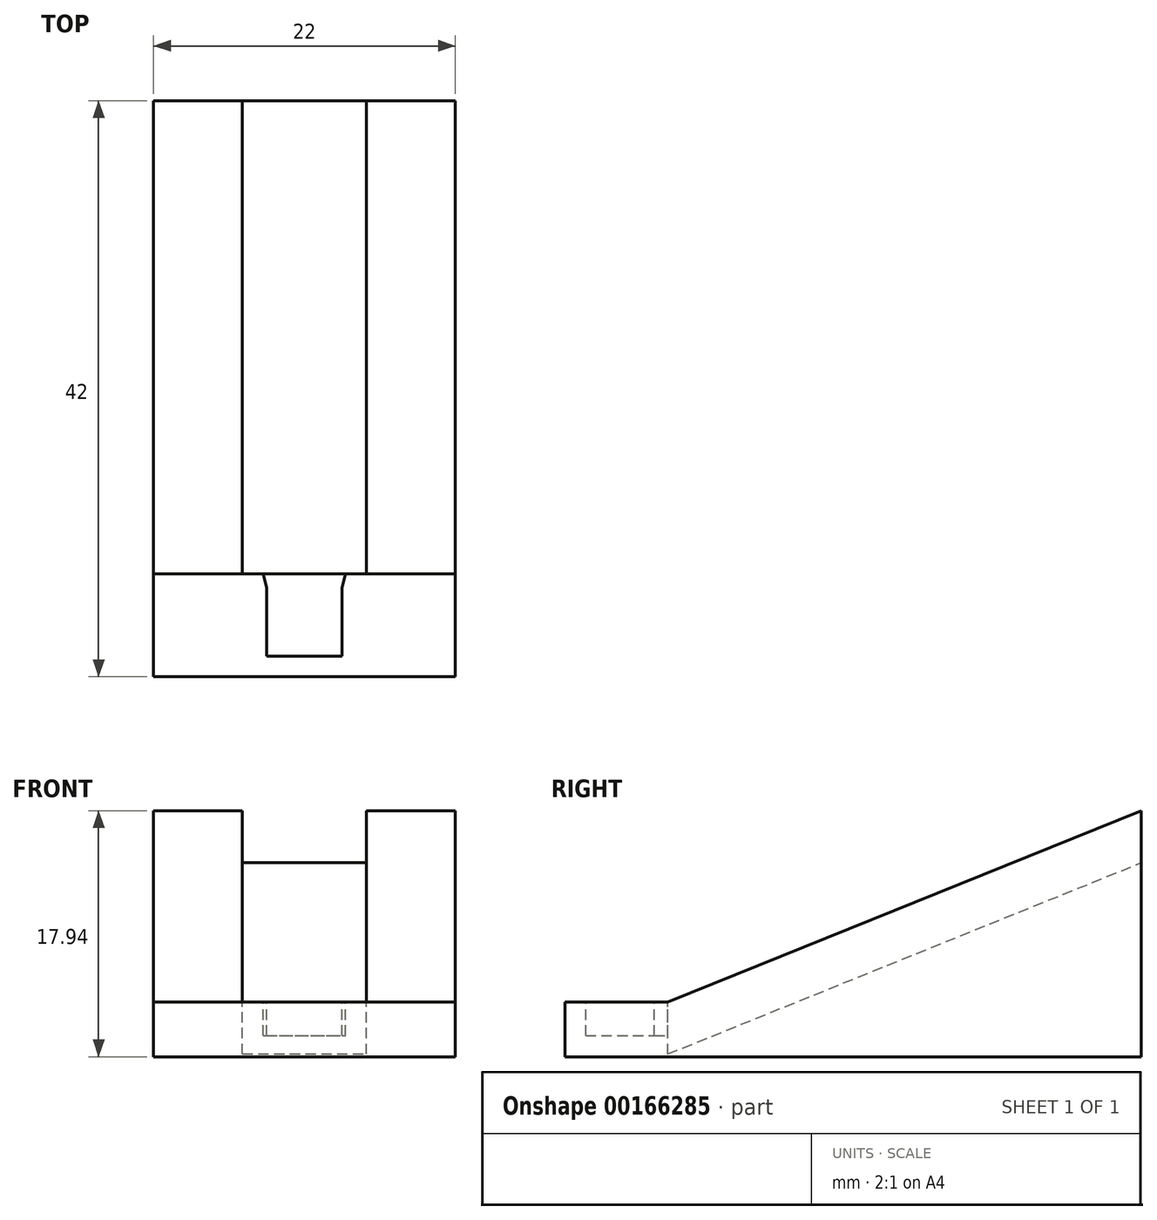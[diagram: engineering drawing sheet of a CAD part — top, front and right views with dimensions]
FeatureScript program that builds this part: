
annotation { "Feature Type Name" : "Feature", "Feature Type Description" : "" }
export const myFeature = defineFeature(function(context is Context, id is Id, definition is map)
    precondition{}
    {
        {
            var Q0;
            Q0=qCreatedBy(makeId("Top.planeOp"),FACE);
            var sketch = newSketch(context, id + "F0", { "sketchPlane" : qUnion([Q0])});
            skLineSegment(sketch, "E0", {"start": v(0, 0) * mm, "end": v(22, 0) * mm});
            skLineSegment(sketch, "E1", {"start": v(22, 0) * mm, "end": v(22, 42) * mm});
            skLineSegment(sketch, "E2", {"start": v(22, 42) * mm, "end": v(0, 42) * mm});
            skLineSegment(sketch, "E3", {"start": v(0, 42) * mm, "end": v(0, 0) * mm});
            skSolve(sketch);
        }
        {
            var Q0;
            Q0=makeQuery(id+"F0.imprint","IMPRINT",FACE,{"disambiguationData":[TD([[makeQuery(id+"F0.imprint","IMPRINT",EDGE,{"derivedFrom":sQuery(id+"F0.wireOp",EDGE,"E0")}),1.0]])]});
            extrude(context, id + "F1", {"entities" : qUnion([Q0]), "depth" : 4 * mm});
        }
        {
            var Q0;
            Q0=makeQuery(id+"F1.opExtrude","CAP_FACE",FACE,{"disambiguationData":[OSD([sQuery(id+"F0.wireOp",EDGE,"E0"),sQuery(id+"F0.wireOp",EDGE,"E1"),sQuery(id+"F0.wireOp",EDGE,"E2"),sQuery(id+"F0.wireOp",EDGE,"E3")])],"isStart":false});
            var sketch = newSketch(context, id + "F2", { "sketchPlane" : qUnion([Q0])});
            skLineSegment(sketch, "E4", {"start": v(8.25, 1.5) * mm, "end": v(8.25, 6.5) * mm});
            skLineSegment(sketch, "E5", {"start": v(13.75, 6.5) * mm, "end": v(13.75, 1.5) * mm});
            skLineSegment(sketch, "E6", {"start": v(8.25, 1.5) * mm, "end": v(13.75, 1.5) * mm});
            skLineSegment(sketch, "E7", {"start": v(8, 7.5) * mm, "end": v(14, 7.5) * mm});
            skLineSegment(sketch, "E8", {"start": v(8, 7.5) * mm, "end": v(8.25, 6.5) * mm});
            skLineSegment(sketch, "E9", {"start": v(13.75, 6.5) * mm, "end": v(14, 7.5) * mm});
            skSolve(sketch);
        }
        {
            var Q0;
            Q0=makeQuery(id+"F2.imprint","IMPRINT",FACE,{"disambiguationData":[TD([[makeQuery(id+"F2.imprint","IMPRINT",EDGE,{"derivedFrom":sQuery(id+"F2.wireOp",EDGE,"E4")}),-1.0]])]});
            extrude(context, id + "F3", {"entities" : qUnion([Q0]), "operationType" : NewBodyOperationType.REMOVE, "oppositeDirection" : true, "depth" : 2.45 * mm});
        }
        {
            var Q0;
            Q0=makeQuery(id+"F1.opExtrude","CAP_FACE",FACE,{"disambiguationData":[OSD([sQuery(id+"F0.wireOp",EDGE,"E0"),sQuery(id+"F0.wireOp",EDGE,"E1"),sQuery(id+"F0.wireOp",EDGE,"E2"),sQuery(id+"F0.wireOp",EDGE,"E3")])],"isStart":false});
            var sketch = newSketch(context, id + "F4", { "sketchPlane" : qUnion([Q0])});
            skLineSegment(sketch, "E10", {"start": v(11, 7.5) * mm, "end": v(15.52, 7.5) * mm});
            skLineSegment(sketch, "E11", {"start": v(11, 7.5) * mm, "end": v(6.48, 7.5) * mm});
            skLineSegment(sketch, "E12", {"start": v(15.52, 7.5) * mm, "end": v(15.52, 42) * mm});
            skLineSegment(sketch, "E13", {"start": v(6.48, 7.5) * mm, "end": v(6.48, 42) * mm});
            skSolve(sketch);
        }
        {
            var Q0;
            {var subQ6=sQuery(id+"F4.wireOp",EDGE,"E12");Q0=makeQuery(id+"F4.imprint","IMPRINT",FACE,{"disambiguationData":[TD([[makeQuery(id+"F4.imprint","IMPRINT",EDGE,{"derivedFrom":subQ6}),1.0]])]});}
            extrude(context, id + "F5", {"entities" : qUnion([Q0]), "operationType" : NewBodyOperationType.REMOVE, "oppositeDirection" : true, "depth" : 3.8 * mm});
        }
        {
            var Q0;
            Q0=makeQuery(id+"F5.boolean.opBoolean","COPY",FACE,{"derivedFrom":makeQuery(id+"F5.opExtrude","SWEPT_FACE",FACE,{"disambiguationData":[OSD([sQuery(id+"F4.wireOp",EDGE,"E13")])]})});
            var sketch = newSketch(context, id + "F6", { "sketchPlane" : qUnion([Q0])});
            skLineSegment(sketch, "E14", {"start": v(7.5, 0.2) * mm, "end": v(42, 14.14) * mm});
            skLineSegment(sketch, "E15", {"start": v(7.5, 0.2) * mm, "end": v(36.42, 0.2) * mm});
            skLineSegment(sketch, "E16", {"start": v(36.42, 0.2) * mm, "end": v(42, 0.2) * mm});
            skLineSegment(sketch, "E17", {"start": v(42, 0.2) * mm, "end": v(42, 14.14) * mm});
            skSolve(sketch);
        }
        {
            var Q0;
            {var subQ0=sQuery(id+"F6.wireOp",EDGE,"E17");var subQ1=sQuery(id+"F6.wireOp",EDGE,"E14");var subQ2=makeQuery(id+"F6.imprint","INTERSECT",VERTEX,{"derivedFrom":[subQ1,subQ0]});Q0=makeQuery(id+"F6.imprint","IMPRINT",FACE,{"disambiguationData":[TD([[makeQuery(id+"F6.imprint","IMPRINT",EDGE,{"disambiguationData":[TD([[subQ2,1.0]])],"derivedFrom":subQ1}),-1.0]])]});}
            var Q1;
            {var subQ5=sQuery(id+"F6.wireOp",EDGE,"E15");Q1=makeQuery(id+"F6.imprint","IMPRINT",FACE,{"disambiguationData":[TD([[makeQuery(id+"F6.imprint","IMPRINT",EDGE,{"derivedFrom":subQ5}),1.0]])]});}
            extrude(context, id + "F7", {"entities" : qUnion([Q0, Q1]), "operationType" : NewBodyOperationType.ADD, "depth" : 9.04 * mm});
        }
        {
            var Q0;
            Q0=makeQuery(id+"F7.opExtrude","CAP_FACE",FACE,{"disambiguationData":[OSD([sQuery(id+"F6.wireOp",EDGE,"E14"),sQuery(id+"F6.wireOp",EDGE,"E15"),sQuery(id+"F6.wireOp",EDGE,"E16"),sQuery(id+"F6.wireOp",EDGE,"E17")])],"isStart":false});
            var sketch = newSketch(context, id + "F8", { "sketchPlane" : qUnion([Q0])});
            skLineSegment(sketch, "E18", {"start": v(42, 14.14) * mm, "end": v(42, 17.94) * mm});
            skLineSegment(sketch, "E19", {"start": v(42, 17.94) * mm, "end": v(7.5, 4) * mm});
            skLineSegment(sketch, "E20", {"start": v(7.5, 4) * mm, "end": v(42, 4) * mm});
            skLineSegment(sketch, "E21", {"start": v(42, 4) * mm, "end": v(42, 14.14) * mm});
            skSolve(sketch);
        }
        {
            var Q0;
            Q0=makeQuery(id+"F8.imprint","IMPRINT",FACE,{"disambiguationData":[TD([[makeQuery(id+"F8.imprint","IMPRINT",EDGE,{"derivedFrom":sQuery(id+"F8.wireOp",EDGE,"E18")}),1.0]])]});
            var Q1;
            {var subQ0=sQuery(id+"F8.wireOp",EDGE,"E21");Q1=makeQuery(id+"F8.imprint","IMPRINT",FACE,{"disambiguationData":[TD([[makeQuery(id+"F8.imprint","IMPRINT",EDGE,{"derivedFrom":subQ0}),1.0]])]});}
            extrude(context, id + "F9", {"entities" : qUnion([Q0, Q1]), "operationType" : NewBodyOperationType.ADD, "depth" : 6.48 * mm});
        }
        {
            var Q0;
            Q0=makeQuery(id+"F7.opExtrude","CAP_FACE",FACE,{"disambiguationData":[OSD([sQuery(id+"F6.wireOp",EDGE,"E14"),sQuery(id+"F6.wireOp",EDGE,"E15"),sQuery(id+"F6.wireOp",EDGE,"E16"),sQuery(id+"F6.wireOp",EDGE,"E17")])],"isStart":true});
            var sketch = newSketch(context, id + "F10", { "sketchPlane" : qUnion([Q0])});
            skLineSegment(sketch, "E22", {"start": v(-42, 14.14) * mm, "end": v(-42, 17.94) * mm});
            skLineSegment(sketch, "E23", {"start": v(-42, 17.94) * mm, "end": v(-7.5, 4) * mm});
            skLineSegment(sketch, "E24", {"start": v(-7.5, 4) * mm, "end": v(-42, 4) * mm});
            skLineSegment(sketch, "E25", {"start": v(-42, 4) * mm, "end": v(-42, 14.14) * mm});
            skSolve(sketch);
        }
        {
            var Q0;
            Q0=makeQuery(id+"F10.imprint","IMPRINT",FACE,{"disambiguationData":[TD([[makeQuery(id+"F10.imprint","IMPRINT",EDGE,{"derivedFrom":sQuery(id+"F10.wireOp",EDGE,"E22")}),-1.0]])]});
            var Q1;
            {var subQ0=sQuery(id+"F10.wireOp",EDGE,"E25");Q1=makeQuery(id+"F10.imprint","IMPRINT",FACE,{"disambiguationData":[TD([[makeQuery(id+"F10.imprint","IMPRINT",EDGE,{"derivedFrom":subQ0}),-1.0]])]});}
            extrude(context, id + "F11", {"entities" : qUnion([Q0, Q1]), "operationType" : NewBodyOperationType.ADD, "depth" : 6.48 * mm});
        }
    });
